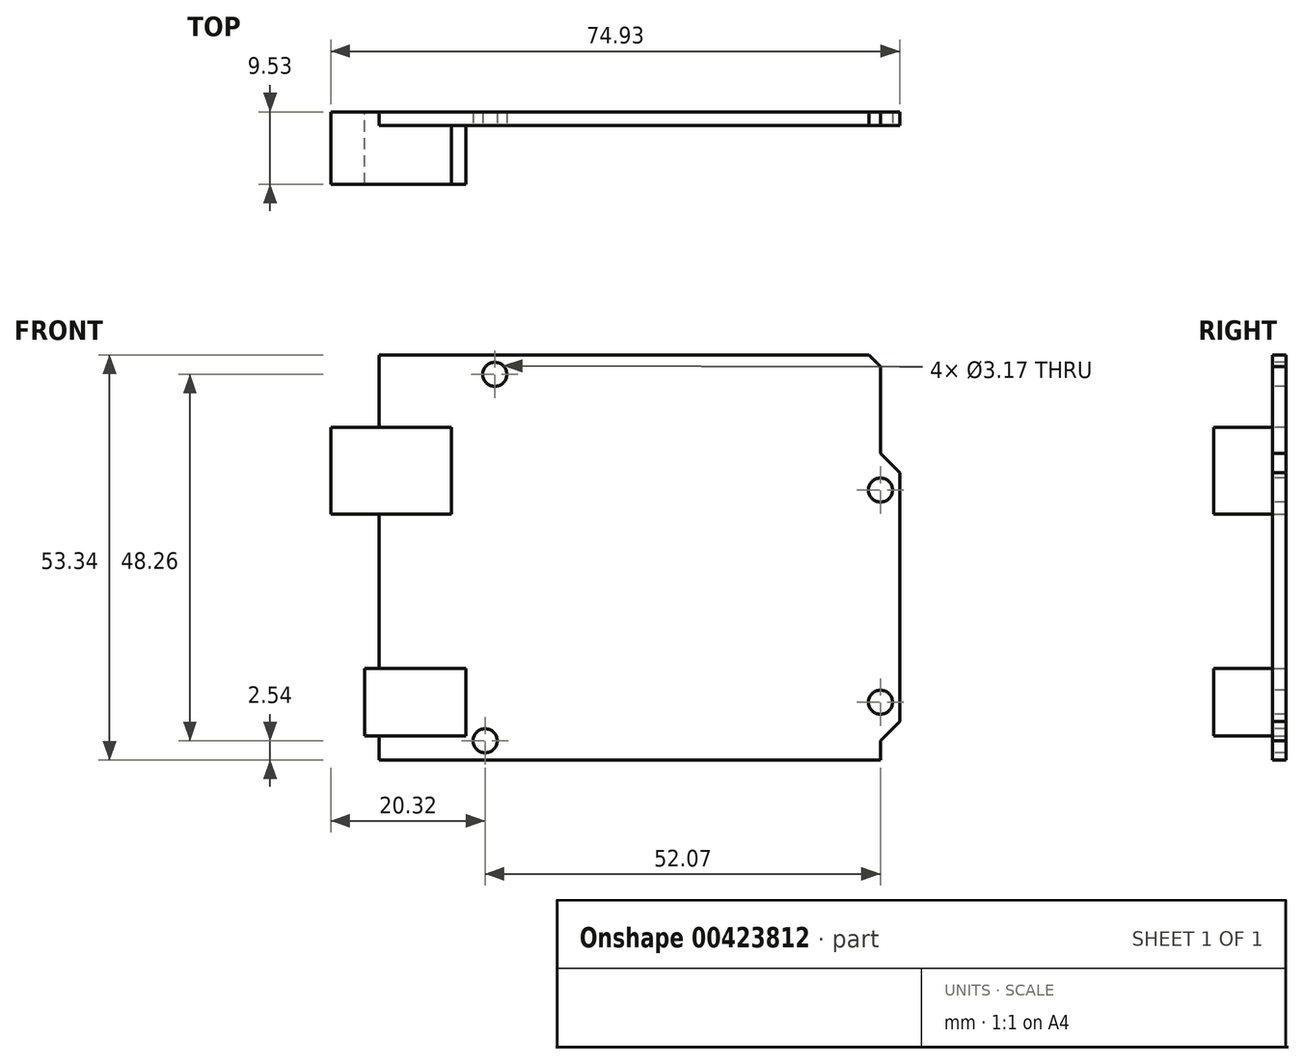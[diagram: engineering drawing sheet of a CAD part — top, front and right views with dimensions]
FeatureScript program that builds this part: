
annotation { "Feature Type Name" : "Feature", "Feature Type Description" : "" }
export const myFeature = defineFeature(function(context is Context, id is Id, definition is map)
    precondition{}
    {
        {
            var Q0;
            Q0=qCreatedBy(makeId("Front.planeOp"),FACE);
            var sketch = newSketch(context, id + "F0", { "sketchPlane" : qUnion([Q0])});
            skLineSegment(sketch, "E0", {"start": v(0, 0) * mm, "end": v(0, 53.34) * mm});
            skLineSegment(sketch, "E1", {"start": v(0, 53.34) * mm, "end": v(64.52, 53.34) * mm});
            skLineSegment(sketch, "E2", {"start": v(64.52, 53.34) * mm, "end": v(66.04, 51.82) * mm});
            skLineSegment(sketch, "E3", {"start": v(66.04, 51.82) * mm, "end": v(66.04, 40.39) * mm});
            skLineSegment(sketch, "E4", {"start": v(68.58, 5.08) * mm, "end": v(68.58, 37.85) * mm});
            skLineSegment(sketch, "E5", {"start": v(66.04, 0) * mm, "end": v(66.04, 2.54) * mm});
            skLineSegment(sketch, "E6", {"start": v(66.04, 2.54) * mm, "end": v(68.58, 5.08) * mm});
            skLineSegment(sketch, "E7", {"start": v(0, 0) * mm, "end": v(66.04, 0) * mm});
            skLineSegment(sketch, "E8", {"start": v(66.04, 40.39) * mm, "end": v(68.58, 37.85) * mm});
            skSolve(sketch);
        }
        {
            var Q0;
            Q0=qCreatedBy(makeId("Front.planeOp"),FACE);
            var sketch = newSketch(context, id + "F1", { "sketchPlane" : qUnion([Q0])});
            skPoint(sketch, "E9", {"position": v(11.43, 3.17) * mm});
            skPoint(sketch, "E10", {"position": v(11.43, 12.07) * mm});
            skPoint(sketch, "E11", {"position": v(-1.9, 3.17) * mm});
            skPoint(sketch, "E12", {"position": v(-1.9, 12.07) * mm});
            skLineSegment(sketch, "E13", {"start": v(11.43, 12.07) * mm, "end": v(11.43, 3.17) * mm});
            skLineSegment(sketch, "E14", {"start": v(-1.9, 3.17) * mm, "end": v(-1.9, 12.07) * mm});
            skPoint(sketch, "E15", {"position": v(9.53, 32.39) * mm});
            skPoint(sketch, "E16", {"position": v(9.52, 43.82) * mm});
            skPoint(sketch, "E17", {"position": v(-6.35, 32.5) * mm});
            skPoint(sketch, "E18", {"position": v(-6.35, 32.39) * mm});
            skLineSegment(sketch, "E19", {"start": v(-6.35, 32.5) * mm, "end": v(-6.35, 32.39) * mm});
            skLineSegment(sketch, "E20", {"start": v(-6.35, 32.39) * mm, "end": v(9.53, 32.39) * mm});
            skLineSegment(sketch, "E21", {"start": v(9.52, 32.39) * mm, "end": v(9.52, 43.82) * mm});
            skPoint(sketch, "E22", {"position": v(23.5, 3.17) * mm});
            skPoint(sketch, "E22.positionSnap0", {"position": v(4.76, 3.17) * mm});
            skLineSegment(sketch, "E23", {"start": v(9.52, 43.82) * mm, "end": v(-6.35, 43.82) * mm});
            skLineSegment(sketch, "E24", {"start": v(-6.35, 43.82) * mm, "end": v(-6.35, 32.5) * mm});
            skLineSegment(sketch, "E25", {"start": v(-1.9, 12.07) * mm, "end": v(11.43, 12.07) * mm});
            skLineSegment(sketch, "E26", {"start": v(-1.9, 3.17) * mm, "end": v(11.43, 3.17) * mm});
            skSolve(sketch);
        }
        {
            var Q0;
            Q0=qSketchRegion(id+"F0",true);
            extrude(context, id + "F2", {"entities" : qUnion([Q0]), "depth" : 1.78 * mm});
        }
        {
            var Q0;
            Q0=qSketchRegion(id+"F1",true);
            extrude(context, id + "F3", {"entities" : qUnion([Q0]), "operationType" : NewBodyOperationType.ADD, "depth" : 9.52 * mm});
        }
        {
            var Q0;
            Q0=makeQuery(id+"F2.opExtrude","CAP_FACE",FACE,{"disambiguationData":[OSD([sQuery(id+"F0.wireOp",EDGE,"E0"),sQuery(id+"F0.wireOp",EDGE,"E1"),sQuery(id+"F0.wireOp",EDGE,"E2"),sQuery(id+"F0.wireOp",EDGE,"E3"),sQuery(id+"F0.wireOp",EDGE,"E4"),sQuery(id+"F0.wireOp",EDGE,"E5"),sQuery(id+"F0.wireOp",EDGE,"E6"),sQuery(id+"F0.wireOp",EDGE,"E7"),sQuery(id+"F0.wireOp",EDGE,"E8")])],"isStart":false});
            var sketch = newSketch(context, id + "F4", { "sketchPlane" : qUnion([Q0])});
            skCircle(sketch, "E27", {"center": v(13.97, 2.54) * mm, "radius": 1.59 * mm});
            skCircle(sketch, "E28", {"center": v(15.24, 50.8) * mm, "radius": 1.59 * mm});
            skCircle(sketch, "E29", {"center": v(66.04, 35.56) * mm, "radius": 1.59 * mm});
            skCircle(sketch, "E30", {"center": v(66.04, 7.62) * mm, "radius": 1.59 * mm});
            skSolve(sketch);
        }
        {
            var Q0;
            Q0=qSketchRegion(id+"F4",true);
            extrude(context, id + "F5", {"entities" : qUnion([Q0]), "operationType" : NewBodyOperationType.REMOVE, "oppositeDirection" : true, "depth" : 25.4 * mm});
        }
    });
